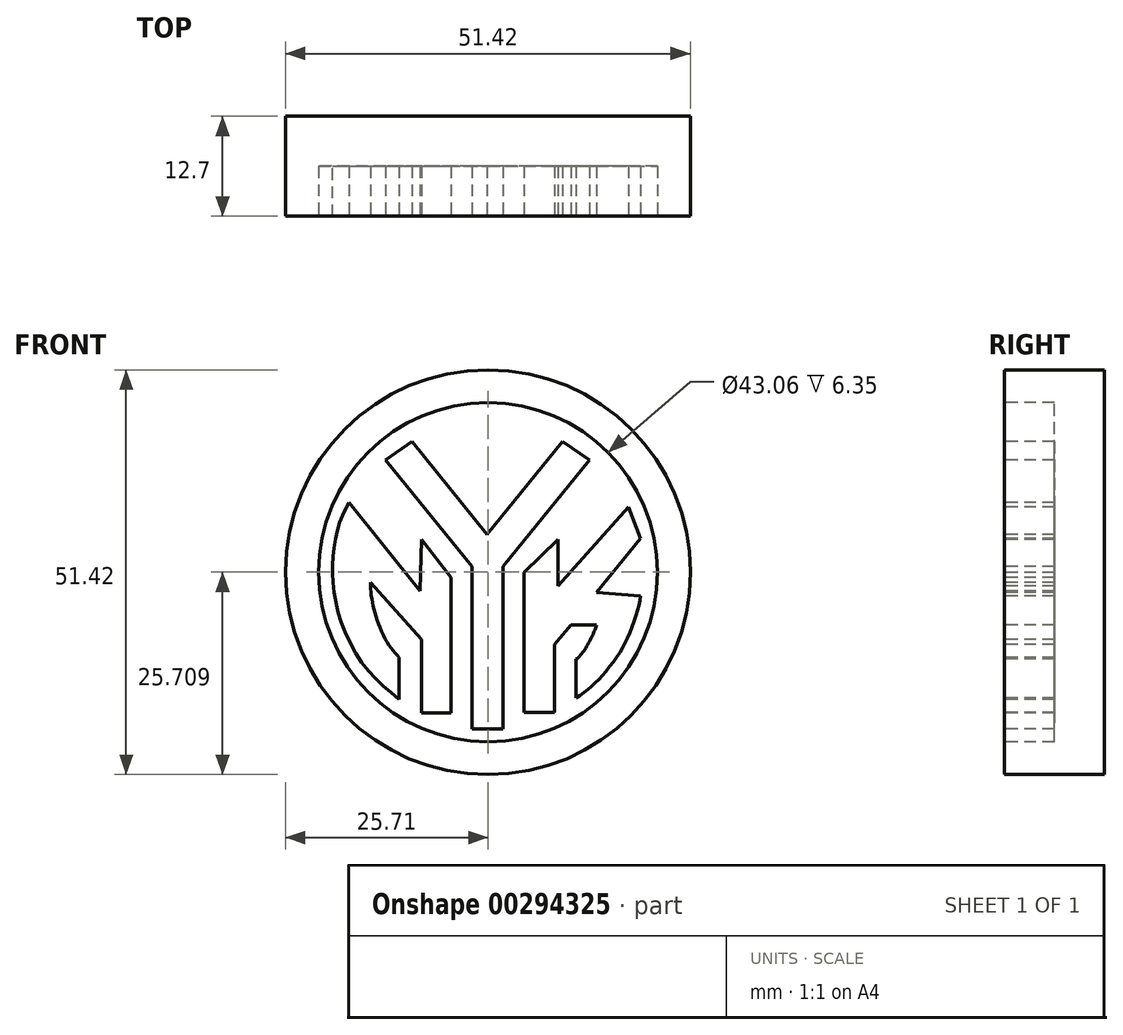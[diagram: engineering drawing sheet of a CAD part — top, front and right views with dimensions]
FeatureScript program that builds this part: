
annotation { "Feature Type Name" : "Feature", "Feature Type Description" : "" }
export const myFeature = defineFeature(function(context is Context, id is Id, definition is map)
    precondition{}
    {
        {
            var Q0;
            Q0=qCreatedBy(makeId("Front.planeOp"),FACE);
            var sketch = newSketch(context, id + "F0", { "sketchPlane" : qUnion([Q0])});
            skCircle(sketch, "E0", {"center": v(-4.1, 0.69) * mm, "radius": 25.7 * mm});
            skCircle(sketch, "E1", {"center": v(-4.1, 0.69) * mm, "radius": 21.53 * mm});
            skLineSegment(sketch, "E2", {"start": v(-21.76, 9.53) * mm, "end": v(-12.72, -1.7) * mm});
            skFitSpline(sketch, "E3", {"points": [v(-17.4, -14.14) * mm, v(-14.62, -17.1) * mm], "startDerivative": vector(2.4, -1.74) * mm, "endDerivative": vector(3.1, -4.04) * mm});
            skPoint(sketch, "E4.4.internal.orphan", {"position": v(-21.76, -8.15) * mm});
            skPoint(sketch, "E5.end.orphan", {"position": v(-18.94, 0) * mm});
            skFitSpline(sketch, "E6", {"points": [v(-21.76, 9.53) * mm, v(-22.53, 8.1) * mm, v(-23.12, 6.46) * mm, v(-23.64, 4.06) * mm, v(-23.84, 1.67) * mm, v(-23.8, -0.64) * mm, v(-23.3, -3.77) * mm, v(-22.27, -6.86) * mm, v(-20.28, -10.61) * mm, v(-17.97, -13.23) * mm, v(-15.38, -15.46) * mm], "startDerivative": vector(-10.6, -18.45) * mm, "endDerivative": vector(23.72, -19.67) * mm});
            skLineSegment(sketch, "E7", {"start": v(-15.38, -15.46) * mm, "end": v(-15.38, -10.16) * mm});
            skFitSpline(sketch, "E8", {"points": [v(-19, -0.6) * mm, v(-18.84, -2.93) * mm, v(-18.12, -5.57) * mm, v(-16.74, -8.52) * mm, v(-15.38, -10.16) * mm], "startDerivative": vector(-0.58, -8.96) * mm, "endDerivative": vector(5.65, -6.99) * mm});
            skLineSegment(sketch, "E9", {"start": v(-6.17, -19.01) * mm, "end": v(-6.17, 1.42) * mm});
            skLineSegment(sketch, "E10", {"start": v(-6.17, 1.42) * mm, "end": v(-17.13, 14.95) * mm});
            skLineSegment(sketch, "E11", {"start": v(-6.17, -19.23) * mm, "end": v(-6.17, -19.01) * mm});
            skLineSegment(sketch, "E12", {"start": v(0.45, 0.69) * mm, "end": v(0.45, -17.11) * mm});
            skLineSegment(sketch, "E13", {"start": v(0.45, -17.11) * mm, "end": v(4.32, -17.11) * mm});
            skLineSegment(sketch, "E14", {"start": v(4.32, -17.11) * mm, "end": v(4.32, -8.5) * mm});
            skLineSegment(sketch, "E15", {"start": v(4.32, -8.5) * mm, "end": v(6.42, -6) * mm});
            skLineSegment(sketch, "E16", {"start": v(6.42, -6) * mm, "end": v(9.68, -6.03) * mm});
            skFitSpline(sketch, "E17", {"points": [v(9.68, -6.03) * mm, v(9.03, -7.6) * mm, v(8.05, -9.35) * mm, v(7.08, -10.35) * mm], "startDerivative": vector(-1.55, -4.94) * mm, "endDerivative": vector(-3.5, -2.37) * mm});
            skLineSegment(sketch, "E18", {"start": v(7.08, -10.35) * mm, "end": v(7.08, -15.31) * mm});
            skFitSpline(sketch, "E19", {"points": [v(7.08, -15.31) * mm, v(8.8, -14) * mm, v(10.46, -12.38) * mm, v(12.34, -9.96) * mm, v(13.68, -7.52) * mm, v(14.76, -4.54) * mm, v(15.26, -2.33) * mm], "startDerivative": vector(11.56, 8.35) * mm, "endDerivative": vector(1.07, 13.87) * mm});
            skLineSegment(sketch, "E20", {"start": v(15.26, -2.33) * mm, "end": v(9.68, -1.86) * mm});
            skLineSegment(sketch, "E21", {"start": v(9.68, -1.86) * mm, "end": v(15.26, 5) * mm});
            skLineSegment(sketch, "E22", {"start": v(15.26, 5) * mm, "end": v(13.75, 9) * mm});
            skLineSegment(sketch, "E23", {"start": v(13.75, 9) * mm, "end": v(4.8, -1.06) * mm});
            skLineSegment(sketch, "E24", {"start": v(4.8, -1.06) * mm, "end": v(4.8, 4.86) * mm});
            skLineSegment(sketch, "E25", {"start": v(4.8, 4.86) * mm, "end": v(0.45, 0.69) * mm});
            skLineSegment(sketch, "E26", {"start": v(-2.2, 1.43) * mm, "end": v(-2.2, -19.23) * mm});
            skLineSegment(sketch, "E27", {"start": v(-2.2, -19.23) * mm, "end": v(-6.17, -19.23) * mm});
            skLineSegment(sketch, "E28", {"start": v(-12.72, -1.7) * mm, "end": v(-12.58, 4.85) * mm});
            skLineSegment(sketch, "E29", {"start": v(-12.58, 4.85) * mm, "end": v(-8.82, 0) * mm});
            skLineSegment(sketch, "E30", {"start": v(-8.82, 0) * mm, "end": v(-8.82, -17.22) * mm});
            skLineSegment(sketch, "E31", {"start": v(-8.82, -17.22) * mm, "end": v(-12.58, -17.22) * mm});
            skLineSegment(sketch, "E32", {"start": v(-12.58, -17.22) * mm, "end": v(-12.58, -7.82) * mm});
            skLineSegment(sketch, "E33", {"start": v(-12.58, -7.82) * mm, "end": v(-19, -0.6) * mm});
            skLineSegment(sketch, "E34", {"start": v(-17.13, 14.95) * mm, "end": v(-13.78, 17.28) * mm});
            skLineSegment(sketch, "E35", {"start": v(-13.78, 17.28) * mm, "end": v(-4.24, 5.47) * mm});
            skLineSegment(sketch, "E36", {"start": v(-4.24, 5.47) * mm, "end": v(5.34, 17.28) * mm});
            skLineSegment(sketch, "E37", {"start": v(5.34, 17.28) * mm, "end": v(8.76, 14.95) * mm});
            skLineSegment(sketch, "E38", {"start": v(8.76, 14.95) * mm, "end": v(-2.2, 1.43) * mm});
            skSolve(sketch);
        }
        {
            var Q0;
            Q0=makeQuery(id+"F0.imprint","IMPRINT",FACE,{"disambiguationData":[TD([[makeQuery(id+"F0.imprint","IMPRINT",EDGE,{"derivedFrom":sQuery(id+"F0.wireOp",EDGE,"E0")}),1.0]])]});
            var Q1;
            Q1=makeQuery(id+"F0.imprint","IMPRINT",FACE,{"disambiguationData":[TD([[makeQuery(id+"F0.imprint","IMPRINT",EDGE,{"derivedFrom":sQuery(id+"F0.wireOp",EDGE,"E1")}),1.0]])]});
            var Q2;
            Q2=makeQuery(id+"F0.imprint","IMPRINT",FACE,{"disambiguationData":[TD([[makeQuery(id+"F0.imprint","IMPRINT",EDGE,{"derivedFrom":sQuery(id+"F0.wireOp",EDGE,"E2")}),-1.0]])]});
            var Q3;
            Q3=makeQuery(id+"F0.imprint","IMPRINT",FACE,{"disambiguationData":[TD([[makeQuery(id+"F0.imprint","IMPRINT",EDGE,{"derivedFrom":sQuery(id+"F0.wireOp",EDGE,"E9")}),-1.0]])]});
            var Q4;
            Q4=makeQuery(id+"F0.imprint","IMPRINT",FACE,{"disambiguationData":[TD([[makeQuery(id+"F0.imprint","IMPRINT",EDGE,{"derivedFrom":sQuery(id+"F0.wireOp",EDGE,"E12")}),1.0]])]});
            extrude(context, id + "F1", {"entities" : qUnion([Q0, Q1, Q2, Q3, Q4]), "oppositeDirection" : true, "depth" : 12.7 * mm});
        }
        {
            var Q0;
            Q0=makeQuery(id+"F0.imprint","IMPRINT",FACE,{"disambiguationData":[TD([[makeQuery(id+"F0.imprint","IMPRINT",EDGE,{"derivedFrom":sQuery(id+"F0.wireOp",EDGE,"E1")}),1.0]])]});
            extrude(context, id + "F2", {"entities" : qUnion([Q0]), "operationType" : NewBodyOperationType.REMOVE, "oppositeDirection" : true, "depth" : 6.35 * mm});
        }
    });
